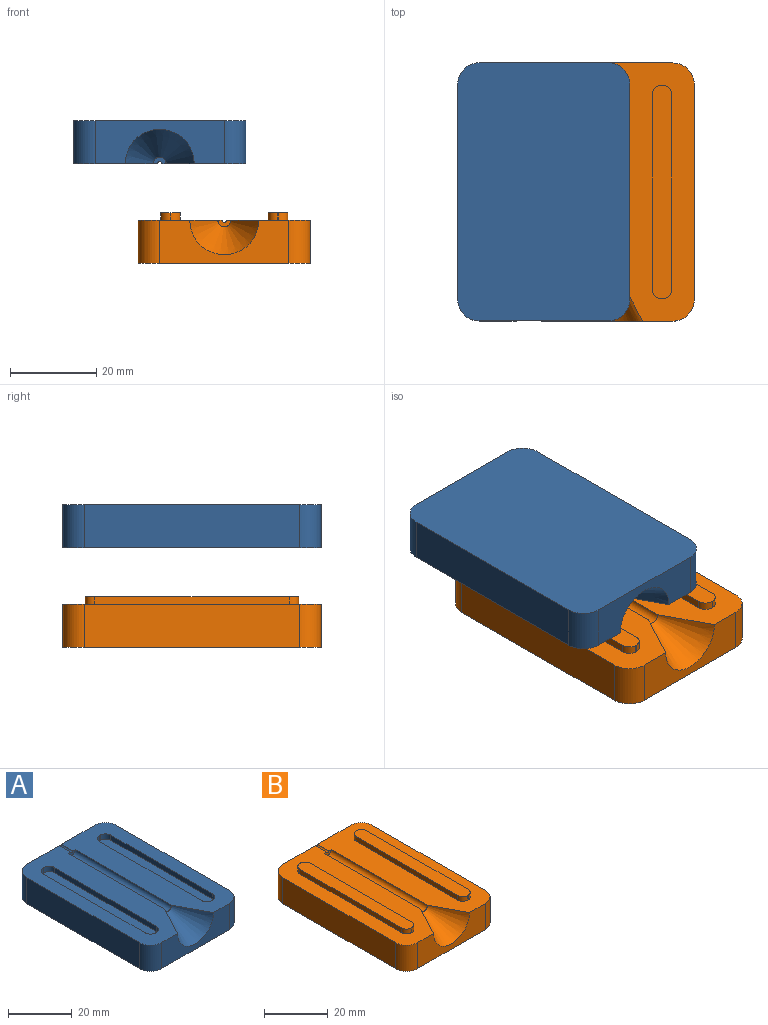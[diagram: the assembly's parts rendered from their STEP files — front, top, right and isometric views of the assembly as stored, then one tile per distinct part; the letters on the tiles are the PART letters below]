
ASSEMBLY  parts=2 mates=3
PART A: 33 faces, bbox 40x60x10 mm
  f0: plane 60x19.5mm, normal (0,0,1), area 819.6mm2, adj f1,f3,f5,f7,f8,f9,f10,f13
  f1: plane 30x10mm, normal (0,-1,0), area 199.5mm2, adj f0,f2,f6,f10,f11,f32
  f2: plane 60x19.5mm, normal (0,0,1), area 819.6mm2, adj f1,f4,f5,f7,f8,f9,f11,f12
  f3: plane 50x10mm, normal (-1,0,0), area 500mm2, adj f0,f6,f10,f13
  f4: plane 50x10mm, normal (1,0,0), area 500mm2, adj f2,f6,f11,f12
  f5: plane 30x10mm, normal (0,1,0), area 299.6mm2, adj f0,f2,f6,f9,f12,f13
  f6: plane 60x40mm, normal (0,0,-1), area 2378.5mm2, adj f1,f3,f4,f5,f10,f11,f12,f13
  f7: cylinder r=1.5mm len=42.81mm, axis (0,-1,0), area 201.7mm2, adj f0,f2,f8,f32
  f8: plane 3x1.5mm, normal (0,-1,0), area 3.1mm2, adj f0,f2,f7,f9
  f9: cylinder r=0.5mm len=5mm, axis (0,1,0), area 7.9mm2, adj f0,f2,f5,f8
  f10: cylinder r=5mm len=10mm, axis (0,0,1), area 78.5mm2, adj f0,f1,f3,f6
  f11: cylinder r=5mm len=10mm, axis (0,0,-1), area 78.5mm2, adj f1,f2,f4,f6
  f12: cylinder r=5mm len=10mm, axis (0,0,1), area 78.5mm2, adj f2,f4,f5,f6
  f13: cylinder r=5mm len=10mm, axis (0,0,-1), area 78.5mm2, adj f0,f3,f5,f6
  f14: plane 45.2x2mm, normal (1,0,0), area 90.4mm2, adj f2,f15,f21,f22
  f15: cylinder r=2.4mm len=2.4mm, axis (0,0,1), area 7.5mm2, adj f2,f14,f16,f22
  f16: plane 2x0.2mm, normal (0,1,0), area 0.4mm2, adj f2,f15,f17,f22
  f17: cylinder r=2.4mm len=2.4mm, axis (0,0,1), area 7.5mm2, adj f2,f16,f18,f22
  f18: plane 45.2x2mm, normal (-1,0,0), area 90.4mm2, adj f2,f17,f19,f22
  f19: cylinder r=2.4mm len=2.4mm, axis (0,0,1), area 7.5mm2, adj f2,f18,f20,f22
  f20: plane 2x0.2mm, normal (0,-1,0), area 0.4mm2, adj f2,f19,f21,f22
  f21: cylinder r=2.4mm len=2.4mm, axis (0,0,1), area 7.5mm2, adj f2,f14,f20,f22
  f22: plane 50x5mm, normal (0,0,1), area 245.1mm2, adj f14,f15,f16,f17,f18,f19,f20,f21
  f23: plane 45.2x2mm, normal (-1,0,0), area 90.4mm2, adj f0,f24,f30,f31
  f24: cylinder r=2.4mm len=2.4mm, axis (0,0,1), area 7.5mm2, adj f0,f23,f25,f31
  f25: plane 2x0.2mm, normal (0,-1,0), area 0.4mm2, adj f0,f24,f26,f31
  f26: cylinder r=2.4mm len=2.4mm, axis (0,0,1), area 7.5mm2, adj f0,f25,f27,f31
  f27: plane 45.2x2mm, normal (1,0,0), area 90.4mm2, adj f0,f26,f28,f31
  f28: cylinder r=2.4mm len=2.4mm, axis (0,0,1), area 7.5mm2, adj f0,f27,f29,f31
  f29: plane 2x0.2mm, normal (0,1,0), area 0.4mm2, adj f0,f28,f30,f31
  f30: cylinder r=2.4mm len=2.4mm, axis (0,0,1), area 7.5mm2, adj f0,f23,f29,f31
  f31: plane 50x5mm, normal (0,0,1), area 245.1mm2, adj f23,f24,f25,f26,f27,f28,f29,f30
  f32: cone r=1.5mm half-angle=28.1deg, axis (0,-1,0), area 206.1mm2, adj f0,f1,f2,f7
PART B: 33 faces, bbox 40x60x11.8 mm
  f0: plane 60x19.5mm, normal (0,0,1), area 840.7mm2, adj f2,f4,f5,f7,f8,f9,f11,f12
  f1: plane 60x19.5mm, normal (0,0,1), area 840.7mm2, adj f2,f3,f5,f7,f8,f9,f10,f13
  f2: plane 30x10mm, normal (0,-1,0), area 199.5mm2, adj f0,f1,f6,f10,f11,f32
  f3: plane 50x10mm, normal (-1,0,0), area 500mm2, adj f1,f6,f10,f13
  f4: plane 50x10mm, normal (1,0,0), area 500mm2, adj f0,f6,f11,f12
  f5: plane 30x10mm, normal (0,1,0), area 299.6mm2, adj f0,f1,f6,f9,f12,f13
  f6: plane 60x40mm, normal (0,0,-1), area 2378.5mm2, adj f2,f3,f4,f5,f10,f11,f12,f13
  f7: cylinder r=1.5mm len=42.81mm, axis (0,-1,0), area 201.7mm2, adj f0,f1,f8,f32
  f8: plane 3x1.5mm, normal (0,-1,0), area 3.1mm2, adj f0,f1,f7,f9
  f9: cylinder r=0.5mm len=5mm, axis (0,1,0), area 7.9mm2, adj f0,f1,f5,f8
  f10: cylinder r=5mm len=10mm, axis (0,0,1), area 78.5mm2, adj f1,f2,f3,f6
  f11: cylinder r=5mm len=10mm, axis (0,0,-1), area 78.5mm2, adj f0,f2,f4,f6
  f12: cylinder r=5mm len=10mm, axis (0,0,1), area 78.5mm2, adj f0,f4,f5,f6
  f13: cylinder r=5mm len=10mm, axis (0,0,-1), area 78.5mm2, adj f1,f3,f5,f6
  f14: plane 1.8x0.2mm, normal (0,1,0), area 0.4mm2, adj f1,f15,f21,f22
  f15: cylinder r=2.2mm len=2.2mm, axis (0,0,-1), area 6.2mm2, adj f1,f14,f16,f22
  f16: plane 45.2x1.8mm, normal (-1,0,0), area 81.4mm2, adj f1,f15,f17,f22
  f17: cylinder r=2.2mm len=2.2mm, axis (0,0,-1), area 6.2mm2, adj f1,f16,f18,f22
  f18: plane 1.8x0.2mm, normal (0,-1,0), area 0.4mm2, adj f1,f17,f19,f22
  f19: cylinder r=2.2mm len=2.2mm, axis (0,0,-1), area 6.2mm2, adj f1,f18,f20,f22
  f20: plane 45.2x1.8mm, normal (1,0,0), area 81.4mm2, adj f1,f19,f21,f22
  f21: cylinder r=2.2mm len=2.2mm, axis (0,0,-1), area 6.2mm2, adj f1,f14,f20,f22
  f22: plane 49.6x4.6mm, normal (0,0,1), area 224mm2, adj f14,f15,f16,f17,f18,f19,f20,f21
  f23: plane 45.2x1.8mm, normal (1,0,0), area 81.4mm2, adj f0,f24,f30,f31
  f24: cylinder r=2.2mm len=2.2mm, axis (0,0,-1), area 6.2mm2, adj f0,f23,f25,f31
  f25: plane 1.8x0.2mm, normal (0,1,0), area 0.4mm2, adj f0,f24,f26,f31
  f26: cylinder r=2.2mm len=2.2mm, axis (0,0,-1), area 6.2mm2, adj f0,f25,f27,f31
  f27: plane 45.2x1.8mm, normal (-1,0,0), area 81.4mm2, adj f0,f26,f28,f31
  f28: cylinder r=2.2mm len=2.2mm, axis (0,0,-1), area 6.2mm2, adj f0,f27,f29,f31
  f29: plane 1.8x0.2mm, normal (0,-1,0), area 0.4mm2, adj f0,f28,f30,f31
  f30: cylinder r=2.2mm len=2.2mm, axis (0,0,-1), area 6.2mm2, adj f0,f23,f29,f31
  f31: plane 49.6x4.6mm, normal (0,0,1), area 224mm2, adj f23,f24,f25,f26,f27,f28,f29,f30
  f32: cone r=1.5mm half-angle=28.1deg, axis (0,-1,0), area 206.1mm2, adj f0,f1,f2,f7
PLACE A rot(axis=(0,1,0),180deg) t=(61.78,-26.26,1.66)mm
PLACE B rot(axis=(0,0,-1),0deg) t=(36.78,-26.26,-31.54)mm
MATE parallel A.f5 <-> B.f5  axis (0,1,0) through (41.78,33.74,-3.34)mm
MATE parallel A.f1 <-> B.f2  axis (0,-1,0) through (41.78,-26.26,-2.54)mm
MATE parallel A.f0 <-> B.f1  axis (0,0,-1) through (43.28,-14.07,-8.34)mm
